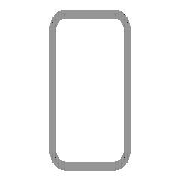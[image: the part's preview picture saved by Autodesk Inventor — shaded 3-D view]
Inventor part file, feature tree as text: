
AUTODESK INVENTOR PART (.ipt)
format: ipt  version: 2025 (Build 290162010, 162A)  size: 152,064 bytes
history: native  units: mm (DEFAULTED — no unit token found)
features: other x4, plane x3, split x2, sketch x1
ambient origin geometry x8: Origin, YZ Plane, XZ Plane, XY Plane, X Axis, Y Axis, Z Axis, Center Point
bodies: Solid1 (feature_tree), Body (feature_tree)
feature tree (10):
  parser-record x1  (decoder bookkeeping rows leaked as tree rows — omitted from the tree; the rows remain in map.json)
  other  "Driven Length"
  other  "Start Plane"
  other  "End Plane"
  plane  "Work Plane4"
  split  "Split1"
  plane  "Work Plane5"
  split  "Split2"
  sketch  "Sketch3"  dims[d3=615.253612mm d4=0.0mm d7=4.0mm d9=20.0mm d11=40.0mm d12=2.0mm d13=-6.618856mm d14=608.634757mm d15=10.0mm d16=20.0mm d17=90.0deg d18=615.253612mm]
  plane  "Work Plane3"
